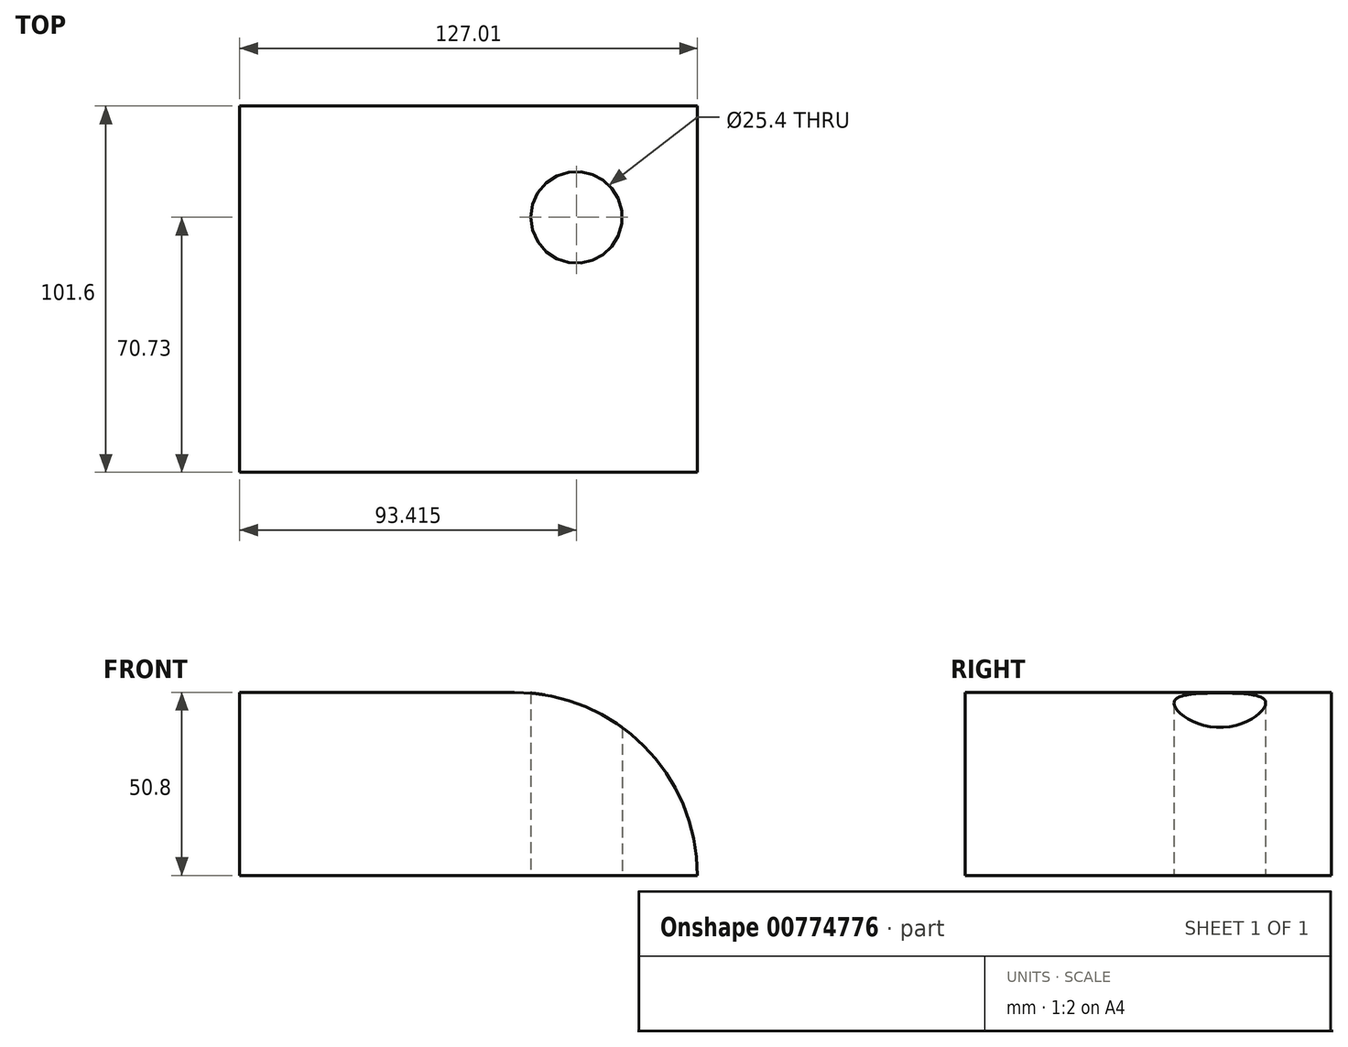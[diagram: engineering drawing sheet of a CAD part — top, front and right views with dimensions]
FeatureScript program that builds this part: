
annotation { "Feature Type Name" : "Feature", "Feature Type Description" : "" }
export const myFeature = defineFeature(function(context is Context, id is Id, definition is map)
    precondition{}
    {
        {
            var Q0;
            Q0=qCreatedBy(makeId("Front.planeOp"),FACE);
            var sketch = newSketch(context, id + "F0", { "sketchPlane" : qUnion([Q0])});
            skLineSegment(sketch, "E0.bottom", {"start": v(0, 0) * mm, "end": v(77.66, 0) * mm});
            skLineSegment(sketch, "E0.top", {"start": v(0, 11.81) * mm, "end": v(77.66, 11.81) * mm});
            skLineSegment(sketch, "E0.left", {"start": v(0, 0) * mm, "end": v(0, 11.81) * mm});
            skLineSegment(sketch, "E0.right", {"start": v(77.66, 0) * mm, "end": v(77.66, 11.81) * mm});
            skSolve(sketch);
        }
        {
            var Q0;
            Q0 = qSketchRegion(id + "F0", true);
            extrude(context, id + "F1", {"entities" : qUnion([Q0]), "depth" : 101.6 * mm, "offsetDistance" : 25.4 * mm});
        }
        {
            var Q0;
            Q0=makeQuery(id+"F1.opExtrude","SWEPT_FACE",FACE,{"disambiguationData":[OSD([sQuery(id+"F0.wireOp",EDGE,"E0.top")])]});
            extrude(context, id + "F2", {"entities" : qUnion([Q0]), "operationType" : NewBodyOperationType.ADD, "depth" : 39 * mm, "offsetDistance" : 25.4 * mm});
        }
        {
            var Q0;
            {var subQ0=sQuery(id+"F0.wireOp",EDGE,"E0.right");Q0=makeQuery(id+"F2.boolean.opBoolean","MERGE",FACE,{"derivedFrom":[makeQuery(id+"F1.opExtrude","SWEPT_FACE",FACE,{"disambiguationData":[OSD([subQ0])]}),makeQuery(id+"F2.opExtrude","SWEPT_FACE",FACE,{"disambiguationData":[OSD([sQuery(id+"F0.wireOp",EDGE,"E0.top"),subQ0])]})]});}
            extrude(context, id + "F3", {"entities" : qUnion([Q0]), "operationType" : NewBodyOperationType.REMOVE, "oppositeDirection" : true, "depth" : 1.45 * mm, "offsetDistance" : 25.4 * mm});
        }
        {
            var Q0;
            Q0=makeQuery(id+"F3.boolean.opBoolean","COPY",FACE,{"derivedFrom":makeQuery(id+"F3.opExtrude","CAP_FACE",FACE,{"disambiguationData":[OSD([sQuery(id+"F0.wireOp",EDGE,"E0.top"),sQuery(id+"F0.wireOp",EDGE,"E0.right")])],"isStart":false})});
            extrude(context, id + "F4", {"entities" : qUnion([Q0]), "operationType" : NewBodyOperationType.ADD, "depth" : 50.8 * mm, "offsetDistance" : 25.4 * mm});
        }
        {
            var Q0;
            {var subQ0=sQuery(id+"F0.wireOp",EDGE,"E0.right");var subQ1=sQuery(id+"F0.wireOp",EDGE,"E0.top");Q0=makeQuery(id+"F4.opExtrude","CAP_EDGE",EDGE,{"disambiguationData":[OSD([subQ1,subQ0]),TDD([makeQuery(id+"F3.boolean.opBoolean","COPY",EDGE,{"derivedFrom":makeQuery(id+"F3.opExtrude","CAP_EDGE",EDGE,{"disambiguationData":[OSD([subQ1,subQ0]),TDD([makeQuery(id+"F2.boolean.opBoolean","MERGE",EDGE,{"derivedFrom":[makeQuery(id+"F1.opExtrude","CAP_EDGE",EDGE,{"disambiguationData":[OSD([subQ0])],"isStart":true}),makeQuery(id+"F2.opExtrude","SWEPT_EDGE",EDGE,{"disambiguationData":[OSD([subQ1,subQ0]),TDD([makeQuery(id+"F1.opExtrude","CAP_VERTEX",VERTEX,{"disambiguationData":[OSD([subQ1,subQ0])],"isStart":true})])]})]})])],"isStart":false})})])],"isStart":false});}
            fillet(context, id + "F5", {"entities" : qUnion([Q0]), "radius" : 50.8 * mm, "tangentPropagation" : true, "allowEdgeOverflow" : false});
        }
        {
            var Q0;
            {var subQ0=sQuery(id+"F0.wireOp",EDGE,"E0.bottom");Q0=makeQuery(id+"F4.boolean.opBoolean","MERGE",FACE,{"derivedFrom":[makeQuery(id+"F1.opExtrude","SWEPT_FACE",FACE,{"disambiguationData":[OSD([subQ0])]}),makeQuery(id+"F4.opExtrude","SWEPT_FACE",FACE,{"disambiguationData":[OSD([subQ0,sQuery(id+"F0.wireOp",EDGE,"E0.right")])]})]});}
            var sketch = newSketch(context, id + "F6", { "sketchPlane" : qUnion([Q0])});
            skCircle(sketch, "E1", {"center": v(93.42, 30.87) * mm, "radius": 23.97 * mm});
            skSolve(sketch);
        }
        {
            var Q0;
            Q0=sQuery(id+"F6.wireOp",VERTEX,"E1.center");
            var Q1;
            Q1=makeQuery(id+"F1.opExtrude","SWEPT_BODY",BODY,{"disambiguationData":[OSD([sQuery(id+"F0.wireOp",EDGE,"E0.bottom"),sQuery(id+"F0.wireOp",EDGE,"E0.top"),sQuery(id+"F0.wireOp",EDGE,"E0.left"),sQuery(id+"F0.wireOp",EDGE,"E0.right")])]});
            hole(context, id + "F7", {"style" : HoleStyle.SIMPLE, "endStyle" : HoleEndStyle.THROUGH, "holeDiameter" : 25.4 * mm, "majorDiameter" : 6.35 * mm, "isTappedThrough" : true, "tappedDepth" : 12.7 * mm, "tapClearance" : 3, "locations" : qUnion([Q0]), "scope" : qUnion([Q1])});
        }
    });
